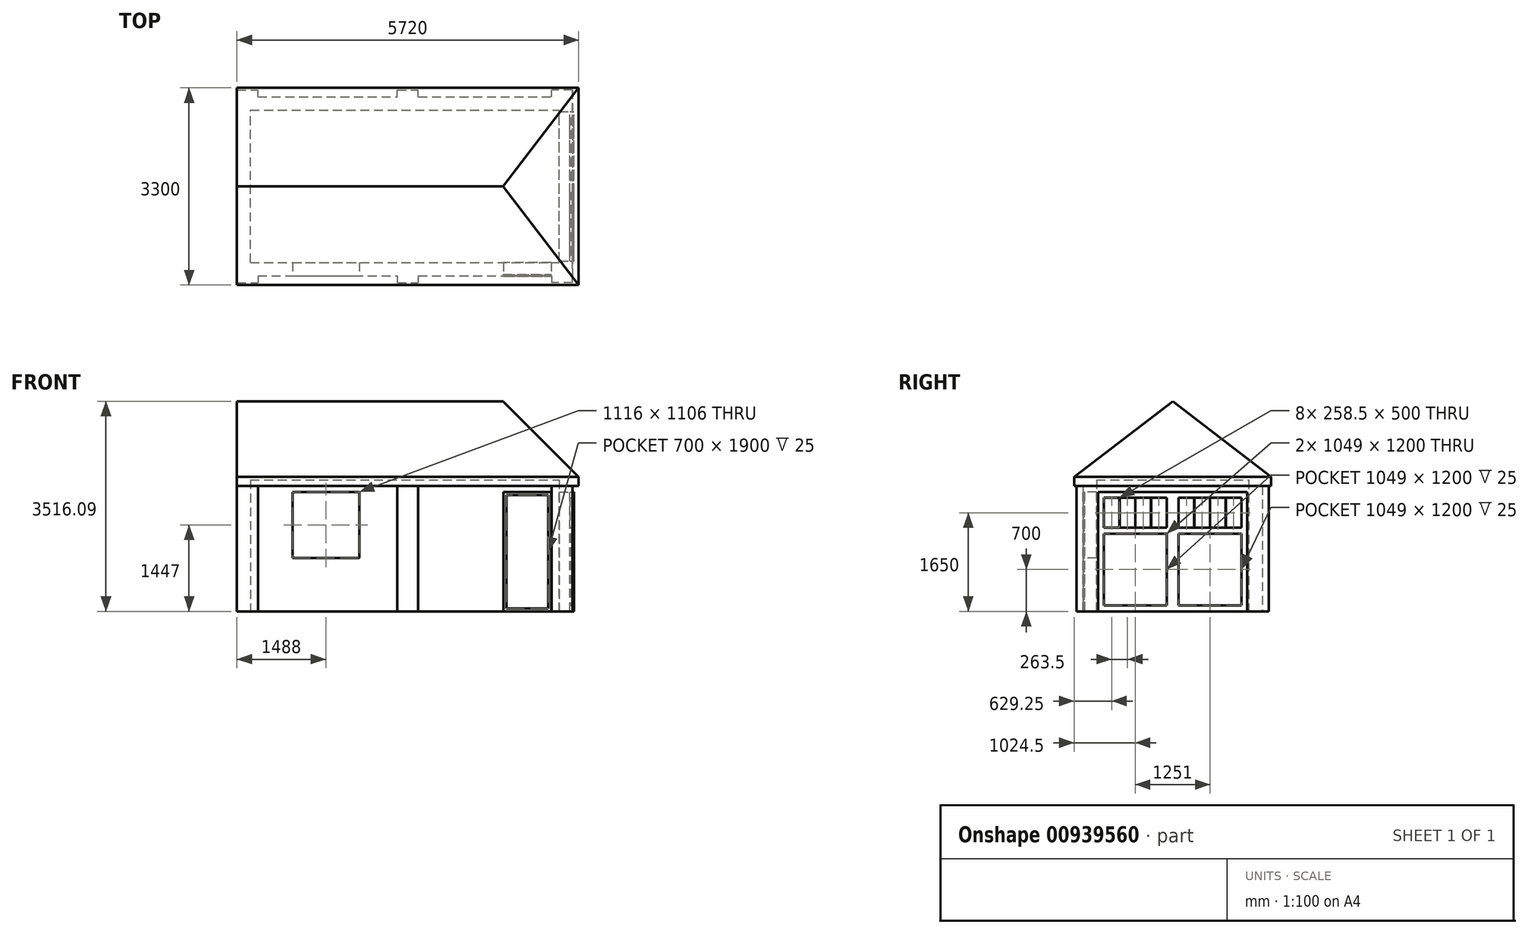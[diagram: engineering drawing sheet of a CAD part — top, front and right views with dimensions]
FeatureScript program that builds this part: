
annotation { "Feature Type Name" : "Feature", "Feature Type Description" : "" }
export const myFeature = defineFeature(function(context is Context, id is Id, definition is map)
    precondition{}
    {
        {
            var Q0;
            Q0=qCreatedBy(makeId("Top.planeOp"),FACE);
            var sketch = newSketch(context, id + "F0", { "sketchPlane" : qUnion([Q0])});
            skLineSegment(sketch, "E0.bottom", {"start": v(0, 0) * mm, "end": v(5620, 0) * mm});
            skLineSegment(sketch, "E0.top", {"start": v(0, 3000) * mm, "end": v(5620, 3000) * mm});
            skLineSegment(sketch, "E0.left", {"start": v(0, 0) * mm, "end": v(0, 3000) * mm});
            skLineSegment(sketch, "E0.right", {"start": v(5620, 0) * mm, "end": v(5620, 3000) * mm});
            skLineSegment(sketch, "E1.bottom", {"start": v(225, 225) * mm, "end": v(5395, 225) * mm});
            skLineSegment(sketch, "E1.top", {"start": v(225, 2775) * mm, "end": v(5395, 2775) * mm});
            skLineSegment(sketch, "E1.left", {"start": v(225, 225) * mm, "end": v(225, 2775) * mm});
            skLineSegment(sketch, "E1.right", {"start": v(5395, 225) * mm, "end": v(5395, 2775) * mm});
            skSolve(sketch);
        }
        {
            var Q0;
            Q0=qSketchRegion(id+"F0",true);
            extrude(context, id + "F1", {"entities" : qUnion([Q0]), "depth" : 2200 * mm, "offsetDistance" : 25 * mm});
        }
        {
            var Q0;
            Q0=makeQuery(id+"F1.opExtrude","SWEPT_FACE",FACE,{"disambiguationData":[OSD([sQuery(id+"F0.wireOp",EDGE,"E0.right")])]});
            var sketch = newSketch(context, id + "F2", { "sketchPlane" : qUnion([Q0])});
            skLineSegment(sketch, "E2.bottom", {"start": v(250, 0) * mm, "end": v(2750, 0) * mm});
            skLineSegment(sketch, "E2.top", {"start": v(250, 2000) * mm, "end": v(2750, 2000) * mm});
            skLineSegment(sketch, "E2.left", {"start": v(250, 0) * mm, "end": v(250, 2000) * mm});
            skLineSegment(sketch, "E2.right", {"start": v(2750, 0) * mm, "end": v(2750, 2000) * mm});
            skSolve(sketch);
        }
        {
            var Q0;
            Q0=qSketchRegion(id+"F2",true);
            extrude(context, id + "F3", {"entities" : qUnion([Q0]), "operationType" : NewBodyOperationType.REMOVE, "endBound" : BoundingType.UP_TO_NEXT, "oppositeDirection" : true, "depth" : 25 * mm, "offsetDistance" : 25 * mm});
        }
        {
            var Q0;
            Q0=makeQuery(id+"F1.opExtrude","SWEPT_FACE",FACE,{"disambiguationData":[OSD([sQuery(id+"F0.wireOp",EDGE,"E0.bottom")])]});
            var sketch = newSketch(context, id + "F4", { "sketchPlane" : qUnion([Q0])});
            skLineSegment(sketch, "E3.bottom", {"start": v(930, 2000) * mm, "end": v(2046, 2000) * mm});
            skLineSegment(sketch, "E3.top", {"start": v(930, 894) * mm, "end": v(2046, 894) * mm});
            skLineSegment(sketch, "E3.left", {"start": v(930, 2000) * mm, "end": v(930, 894) * mm});
            skLineSegment(sketch, "E3.right", {"start": v(2046, 2000) * mm, "end": v(2046, 894) * mm});
            skLineSegment(sketch, "E4.bottom", {"start": v(5260, 0) * mm, "end": v(4460, 0) * mm});
            skLineSegment(sketch, "E4.top", {"start": v(5260, 2000) * mm, "end": v(4460, 2000) * mm});
            skLineSegment(sketch, "E4.left", {"start": v(5260, 0) * mm, "end": v(5260, 2000) * mm});
            skLineSegment(sketch, "E4.right", {"start": v(4460, 0) * mm, "end": v(4460, 2000) * mm});
            skSolve(sketch);
        }
        {
            var Q0;
            Q0=qSketchRegion(id+"F4",true);
            extrude(context, id + "F5", {"entities" : qUnion([Q0]), "operationType" : NewBodyOperationType.REMOVE, "endBound" : BoundingType.UP_TO_NEXT, "oppositeDirection" : true, "depth" : 25 * mm, "offsetDistance" : 25 * mm});
        }
        {
            var Q0;
            Q0=makeQuery(id+"F1.opExtrude","SWEPT_FACE",FACE,{"disambiguationData":[OSD([sQuery(id+"F0.wireOp",EDGE,"E0.bottom")])]});
            cPlane(context, id + "F6", {"entities" : qUnion([Q0]), "cplaneType" : CPlaneType.OFFSET, "offset" : 25 * mm, "oppositeDirection" : true, "width" : 150 * mm, "height" : 150 * mm});
        }
        {
            var Q0;
            Q0=qCreatedBy(id+"F6.planeOp",FACE);
            var sketch = newSketch(context, id + "F7", { "sketchPlane" : qUnion([Q0])});
            skLineSegment(sketch, "E5.bottom", {"start": v(4510, 1950) * mm, "end": v(5210, 1950) * mm});
            skLineSegment(sketch, "E5.top", {"start": v(4510, 50) * mm, "end": v(5210, 50) * mm});
            skLineSegment(sketch, "E5.left", {"start": v(4510, 1950) * mm, "end": v(4510, 50) * mm});
            skLineSegment(sketch, "E5.right", {"start": v(5210, 1950) * mm, "end": v(5210, 50) * mm});
            skLineSegment(sketch, "E6.bottom", {"start": v(4460, 2000) * mm, "end": v(5260, 2000) * mm});
            skLineSegment(sketch, "E6.top", {"start": v(4460, 0) * mm, "end": v(5260, 0) * mm});
            skLineSegment(sketch, "E6.left", {"start": v(4460, 2000) * mm, "end": v(4460, 0) * mm});
            skLineSegment(sketch, "E6.right", {"start": v(5260, 2000) * mm, "end": v(5260, 0) * mm});
            skSolve(sketch);
        }
        {
            var Q0;
            Q0=qSketchRegion(id+"F7",true);
            extrude(context, id + "F8", {"entities" : qUnion([Q0]), "depth" : 30 * mm, "offsetDistance" : 25 * mm});
        }
        {
            var Q0;
            Q0=makeQuery(id+"F7.imprint","IMPRINT",FACE,{"disambiguationData":[TD([[makeQuery(id+"F7.imprint","IMPRINT",EDGE,{"derivedFrom":sQuery(id+"F7.wireOp",EDGE,"E5.bottom")}),-1.0]])]});
            extrude(context, id + "F9", {"entities" : qUnion([Q0]), "operationType" : NewBodyOperationType.ADD, "depth" : 5 * mm, "offsetDistance" : 25 * mm});
        }
        {
            var Q0;
            Q0=makeQuery(id+"F1.opExtrude","SWEPT_FACE",FACE,{"disambiguationData":[OSD([sQuery(id+"F0.wireOp",EDGE,"E0.right")])]});
            var sketch = newSketch(context, id + "F10", { "sketchPlane" : qUnion([Q0])});
            skLineSegment(sketch, "E7", {"start": v(0, 2100) * mm, "end": v(-150, 2100) * mm});
            skLineSegment(sketch, "E8", {"start": v(-150, 2100) * mm, "end": v(-150, 2250) * mm});
            skLineSegment(sketch, "E9", {"start": v(-150, 2250) * mm, "end": v(1500, 3516.09) * mm});
            skLineSegment(sketch, "E10", {"start": v(1500, 3516.09) * mm, "end": v(3150, 2250) * mm});
            skLineSegment(sketch, "E11", {"start": v(3150, 2250) * mm, "end": v(3150, 2100) * mm});
            skLineSegment(sketch, "E12", {"start": v(3150, 2100) * mm, "end": v(3000, 2100) * mm});
            skLineSegment(sketch, "E13", {"start": v(3000, 2100) * mm, "end": v(3000, 2200) * mm});
            skLineSegment(sketch, "E14", {"start": v(3000, 2200) * mm, "end": v(0, 2200) * mm});
            skLineSegment(sketch, "E15", {"start": v(0, 2200) * mm, "end": v(0, 2100) * mm});
            skSolve(sketch);
        }
        {
            var Q0;
            Q0=qSketchRegion(id+"F10",true);
            var Q1;
            Q1=makeQuery(id+"F1.opExtrude","SWEPT_FACE",FACE,{"disambiguationData":[OSD([sQuery(id+"F0.wireOp",EDGE,"E0.left")])]});
            extrude(context, id + "F11", {"entities" : qUnion([Q0]), "operationType" : NewBodyOperationType.ADD, "endBound" : BoundingType.UP_TO_SURFACE, "oppositeDirection" : true, "depth" : 5630 * mm, "endBoundEntityFace" : qUnion([Q1]), "offsetDistance" : 100 * mm, "offsetOppositeDirection" : true, "hasSecondDirection" : true, "secondDirectionOppositeDirection" : false, "secondDirectionDepth" : 100 * mm});
        }
        {
            var Q0;
            {var subQ1=sQuery(id+"F10.wireOp",EDGE,"E14");Q0=makeQuery(id+"F11.boolean.opBoolean","SPLIT",FACE,{"disambiguationData":[TD([makeQuery(id+"F1.opExtrude","SWEPT_FACE",FACE,{"disambiguationData":[OSD([sQuery(id+"F0.wireOp",EDGE,"E0.right")])]})])],"derivedFrom":makeQuery(id+"F11.opExtrude","SWEPT_FACE",FACE,{"disambiguationData":[OSD([subQ1])]})});}
            var Q1;
            Q1=makeQuery(id+"F11.opExtrude","SWEPT_FACE",FACE,{"disambiguationData":[OSD([sQuery(id+"F10.wireOp",EDGE,"E7")])]});
            extrude(context, id + "F12", {"entities" : qUnion([Q0]), "operationType" : NewBodyOperationType.ADD, "endBound" : BoundingType.UP_TO_SURFACE, "depth" : 25 * mm, "endBoundEntityFace" : qUnion([Q1]), "offsetDistance" : 25 * mm});
        }
        {
            var Q0;
            Q0=makeQuery(id+"F11.opExtrude","SWEPT_FACE",FACE,{"disambiguationData":[OSD([sQuery(id+"F10.wireOp",EDGE,"E8")])]});
            var sketch = newSketch(context, id + "F13", { "sketchPlane" : qUnion([Q0])});
            skLineSegment(sketch, "E16", {"start": v(5720, 2250) * mm, "end": v(3720, 4250) * mm});
            skLineSegment(sketch, "E17", {"start": v(3720, 4250) * mm, "end": v(5720, 4250) * mm});
            skLineSegment(sketch, "E18", {"start": v(5720, 4250) * mm, "end": v(5720, 2250) * mm});
            skSolve(sketch);
        }
        {
            var Q0;
            Q0=qSketchRegion(id+"F13",true);
            extrude(context, id + "F14", {"entities" : qUnion([Q0]), "operationType" : NewBodyOperationType.REMOVE, "oppositeDirection" : true, "depth" : 6760 * mm, "offsetDistance" : 25 * mm});
        }
        {
            var Q0;
            {var subQ0=sQuery(id+"F0.wireOp",EDGE,"E0.left");var subQ1=sQuery(id+"F0.wireOp",EDGE,"E0.top");var subQ2=sQuery(id+"F0.wireOp",EDGE,"E0.right");var subQ3=sQuery(id+"F0.wireOp",EDGE,"E0.bottom");var subQ4=sQuery(id+"F0.wireOp",EDGE,"E1.bottom");var subQ5=sQuery(id+"F0.wireOp",EDGE,"E1.top");var subQ6=sQuery(id+"F0.wireOp",EDGE,"E1.left");var subQ7=sQuery(id+"F0.wireOp",EDGE,"E1.right");Q0=makeQuery(id+"F5.boolean.opBoolean","SPLIT",FACE,{"disambiguationData":[TD([makeQuery(id+"F1.opExtrude","SWEPT_FACE",FACE,{"disambiguationData":[OSD([subQ1])]})])],"derivedFrom":makeQuery(id+"F1.opExtrude","CAP_FACE",FACE,{"disambiguationData":[OSD([subQ3,subQ1,subQ0,subQ2,subQ4,subQ5,subQ6,subQ7])],"isStart":true})});}
            var sketch = newSketch(context, id + "F15", { "sketchPlane" : qUnion([Q0])});
            skLineSegment(sketch, "E19.bottom", {"start": v(0, 0) * mm, "end": v(350, 0) * mm});
            skLineSegment(sketch, "E19.top", {"start": v(0, 110) * mm, "end": v(350, 110) * mm});
            skLineSegment(sketch, "E19.left", {"start": v(0, 0) * mm, "end": v(0, 110) * mm});
            skLineSegment(sketch, "E19.right", {"start": v(350, 0) * mm, "end": v(350, 110) * mm});
            skLineSegment(sketch, "E20.bottom", {"start": v(2685, 0) * mm, "end": v(3035, 0) * mm});
            skLineSegment(sketch, "E20.top", {"start": v(2685, 110) * mm, "end": v(3035, 110) * mm});
            skLineSegment(sketch, "E20.left", {"start": v(2685, 0) * mm, "end": v(2685, 110) * mm});
            skLineSegment(sketch, "E20.right", {"start": v(3035, 0) * mm, "end": v(3035, 110) * mm});
            skLineSegment(sketch, "E21.bottom", {"start": v(5620, 0) * mm, "end": v(5270, 0) * mm});
            skLineSegment(sketch, "E21.top", {"start": v(5620, 110) * mm, "end": v(5270, 110) * mm});
            skLineSegment(sketch, "E21.left", {"start": v(5620, 0) * mm, "end": v(5620, 110) * mm});
            skLineSegment(sketch, "E21.right", {"start": v(5270, 0) * mm, "end": v(5270, 110) * mm});
            skLineSegment(sketch, "E22.bottom", {"start": v(0, -3000) * mm, "end": v(350, -3000) * mm});
            skLineSegment(sketch, "E22.top", {"start": v(0, -3110) * mm, "end": v(350, -3110) * mm});
            skLineSegment(sketch, "E22.left", {"start": v(0, -3000) * mm, "end": v(0, -3110) * mm});
            skLineSegment(sketch, "E22.right", {"start": v(350, -3000) * mm, "end": v(350, -3110) * mm});
            skLineSegment(sketch, "E23.bottom", {"start": v(2685, -3000) * mm, "end": v(3035, -3000) * mm});
            skLineSegment(sketch, "E23.top", {"start": v(2685, -3110) * mm, "end": v(3035, -3110) * mm});
            skLineSegment(sketch, "E23.left", {"start": v(2685, -3000) * mm, "end": v(2685, -3110) * mm});
            skLineSegment(sketch, "E23.right", {"start": v(3035, -3000) * mm, "end": v(3035, -3110) * mm});
            skLineSegment(sketch, "E24.bottom", {"start": v(5620, -3000) * mm, "end": v(5270, -3000) * mm});
            skLineSegment(sketch, "E24.top", {"start": v(5620, -3110) * mm, "end": v(5270, -3110) * mm});
            skLineSegment(sketch, "E24.left", {"start": v(5620, -3000) * mm, "end": v(5620, -3110) * mm});
            skLineSegment(sketch, "E24.right", {"start": v(5270, -3000) * mm, "end": v(5270, -3110) * mm});
            skLineSegment(sketch, "E25", {"start": v(2860, 428.34) * mm, "end": v(2860, -3399.48) * mm, "construction": true});
            skSolve(sketch);
        }
        {
            var Q0;
            Q0=qSketchRegion(id+"F15",true);
            var Q1;
            {var subQ0=sQuery(id+"F10.wireOp",EDGE,"E7");Q1=makeQuery(id+"F12.boolean.opBoolean","MERGE",FACE,{"derivedFrom":[makeQuery(id+"F11.opExtrude","SWEPT_FACE",FACE,{"disambiguationData":[OSD([subQ0])]}),makeQuery(id+"F11.opExtrude","SWEPT_FACE",FACE,{"disambiguationData":[OSD([sQuery(id+"F10.wireOp",EDGE,"E12")])]}),makeQuery(id+"F12.opExtrude","CAP_FACE",FACE,{"disambiguationData":[OSD([subQ0])],"isStart":false})]});}
            extrude(context, id + "F16", {"entities" : qUnion([Q0]), "operationType" : NewBodyOperationType.ADD, "endBound" : BoundingType.UP_TO_SURFACE, "oppositeDirection" : true, "depth" : 25 * mm, "endBoundEntityFace" : qUnion([Q1]), "offsetDistance" : 25 * mm});
        }
        {
            var Q0;
            Q0=makeQuery(id+"F16.boolean.opBoolean","MERGE",FACE,{"derivedFrom":[makeQuery(id+"F1.opExtrude","SWEPT_FACE",FACE,{"disambiguationData":[OSD([sQuery(id+"F0.wireOp",EDGE,"E0.right")])]}),makeQuery(id+"F16.opExtrude","SWEPT_FACE",FACE,{"disambiguationData":[OSD([sQuery(id+"F15.wireOp",EDGE,"E21.left")])]}),makeQuery(id+"F16.opExtrude","SWEPT_FACE",FACE,{"disambiguationData":[OSD([sQuery(id+"F15.wireOp",EDGE,"E24.left")])]})]});
            var sketch = newSketch(context, id + "F17", { "sketchPlane" : qUnion([Q0])});
            skLineSegment(sketch, "E26.bottom", {"start": v(250, 2000) * mm, "end": v(2750, 2000) * mm});
            skLineSegment(sketch, "E26.top", {"start": v(250, 0) * mm, "end": v(2750, 0) * mm});
            skLineSegment(sketch, "E26.left", {"start": v(250, 2000) * mm, "end": v(250, 0) * mm});
            skLineSegment(sketch, "E26.right", {"start": v(2750, 2000) * mm, "end": v(2750, 0) * mm});
            skLineSegment(sketch, "E27.bottom", {"start": v(350, 1300) * mm, "end": v(1399, 1300) * mm});
            skLineSegment(sketch, "E27.top", {"start": v(350, 100) * mm, "end": v(1399, 100) * mm});
            skLineSegment(sketch, "E27.left", {"start": v(350, 1300) * mm, "end": v(350, 100) * mm});
            skLineSegment(sketch, "E27.right", {"start": v(1399, 1300) * mm, "end": v(1399, 100) * mm});
            skLineSegment(sketch, "E28.bottom", {"start": v(1601, 1300) * mm, "end": v(2650, 1300) * mm});
            skLineSegment(sketch, "E28.top", {"start": v(1601, 100) * mm, "end": v(2650, 100) * mm});
            skLineSegment(sketch, "E28.left", {"start": v(1601, 1300) * mm, "end": v(1601, 100) * mm});
            skLineSegment(sketch, "E28.right", {"start": v(2650, 1300) * mm, "end": v(2650, 100) * mm});
            skLineSegment(sketch, "E29.bottom", {"start": v(350, 1900) * mm, "end": v(608.5, 1900) * mm});
            skLineSegment(sketch, "E29.top", {"start": v(350, 1400) * mm, "end": v(608.5, 1400) * mm});
            skLineSegment(sketch, "E29.left", {"start": v(350, 1900) * mm, "end": v(350, 1400) * mm});
            skLineSegment(sketch, "E29.right", {"start": v(608.5, 1900) * mm, "end": v(608.5, 1400) * mm});
            skLineSegment(sketch, "E30.bottom", {"start": v(613.5, 1900) * mm, "end": v(872, 1900) * mm});
            skLineSegment(sketch, "E30.top", {"start": v(613.5, 1400) * mm, "end": v(872, 1400) * mm});
            skLineSegment(sketch, "E30.left", {"start": v(613.5, 1900) * mm, "end": v(613.5, 1400) * mm});
            skLineSegment(sketch, "E30.right", {"start": v(872, 1900) * mm, "end": v(872, 1400) * mm});
            skLineSegment(sketch, "E31.bottom", {"start": v(877, 1900) * mm, "end": v(1135.5, 1900) * mm});
            skLineSegment(sketch, "E31.top", {"start": v(877, 1400) * mm, "end": v(1135.5, 1400) * mm});
            skLineSegment(sketch, "E31.left", {"start": v(877, 1900) * mm, "end": v(877, 1400) * mm});
            skLineSegment(sketch, "E31.right", {"start": v(1135.5, 1900) * mm, "end": v(1135.5, 1400) * mm});
            skLineSegment(sketch, "E32.bottom", {"start": v(1140.5, 1900) * mm, "end": v(1399, 1900) * mm});
            skLineSegment(sketch, "E32.top", {"start": v(1140.5, 1400) * mm, "end": v(1399, 1400) * mm});
            skLineSegment(sketch, "E32.left", {"start": v(1140.5, 1900) * mm, "end": v(1140.5, 1400) * mm});
            skLineSegment(sketch, "E32.right", {"start": v(1399, 1900) * mm, "end": v(1399, 1400) * mm});
            skLineSegment(sketch, "E33.bottom", {"start": v(1601, 1400) * mm, "end": v(1859.5, 1400) * mm});
            skLineSegment(sketch, "E33.top", {"start": v(1601, 1900) * mm, "end": v(1859.5, 1900) * mm});
            skLineSegment(sketch, "E33.left", {"start": v(1601, 1400) * mm, "end": v(1601, 1900) * mm});
            skLineSegment(sketch, "E33.right", {"start": v(1859.5, 1400) * mm, "end": v(1859.5, 1900) * mm});
            skLineSegment(sketch, "E34.bottom", {"start": v(1864.5, 1900) * mm, "end": v(2123, 1900) * mm});
            skLineSegment(sketch, "E34.top", {"start": v(1864.5, 1400) * mm, "end": v(2123, 1400) * mm});
            skLineSegment(sketch, "E34.left", {"start": v(1864.5, 1900) * mm, "end": v(1864.5, 1400) * mm});
            skLineSegment(sketch, "E34.right", {"start": v(2123, 1900) * mm, "end": v(2123, 1400) * mm});
            skLineSegment(sketch, "E35.bottom", {"start": v(2128, 1900) * mm, "end": v(2386.5, 1900) * mm});
            skLineSegment(sketch, "E35.top", {"start": v(2128, 1400) * mm, "end": v(2386.5, 1400) * mm});
            skLineSegment(sketch, "E35.left", {"start": v(2128, 1900) * mm, "end": v(2128, 1400) * mm});
            skLineSegment(sketch, "E35.right", {"start": v(2386.5, 1900) * mm, "end": v(2386.5, 1400) * mm});
            skLineSegment(sketch, "E36.bottom", {"start": v(2391.5, 1900) * mm, "end": v(2650, 1900) * mm});
            skLineSegment(sketch, "E36.top", {"start": v(2391.5, 1400) * mm, "end": v(2650, 1400) * mm});
            skLineSegment(sketch, "E36.left", {"start": v(2391.5, 1900) * mm, "end": v(2391.5, 1400) * mm});
            skLineSegment(sketch, "E36.right", {"start": v(2650, 1900) * mm, "end": v(2650, 1400) * mm});
            skLineSegment(sketch, "E37.bottom", {"start": v(1501, 2000) * mm, "end": v(1499, 2000) * mm});
            skLineSegment(sketch, "E37.top", {"start": v(1501, 0) * mm, "end": v(1499, 0) * mm});
            skLineSegment(sketch, "E37.left", {"start": v(1501, 2000) * mm, "end": v(1501, 0) * mm});
            skLineSegment(sketch, "E37.right", {"start": v(1499, 2000) * mm, "end": v(1499, 0) * mm});
            skSolve(sketch);
        }
        {
            var Q0;
            Q0=qSketchRegion(id+"F17",true);
            extrude(context, id + "F18", {"entities" : qUnion([Q0]), "oppositeDirection" : true, "depth" : 50 * mm, "offsetDistance" : 25 * mm, "hasSecondDirection" : true, "secondDirectionOppositeDirection" : false, "secondDirectionDepth" : 25 * mm});
        }
        {
            var Q0;
            Q0=makeQuery(id+"F17.imprint","IMPRINT",FACE,{"disambiguationData":[TD([[makeQuery(id+"F17.imprint","IMPRINT",EDGE,{"derivedFrom":sQuery(id+"F17.wireOp",EDGE,"E27.bottom")}),-1.0]])]});
            var Q1;
            Q1=makeQuery(id+"F17.imprint","IMPRINT",FACE,{"disambiguationData":[TD([[makeQuery(id+"F17.imprint","IMPRINT",EDGE,{"derivedFrom":sQuery(id+"F17.wireOp",EDGE,"E28.bottom")}),-1.0]])]});
            extrude(context, id + "F19", {"entities" : qUnion([Q0, Q1]), "operationType" : NewBodyOperationType.ADD, "oppositeDirection" : true, "depth" : 25 * mm, "offsetDistance" : 25 * mm});
        }
    });
